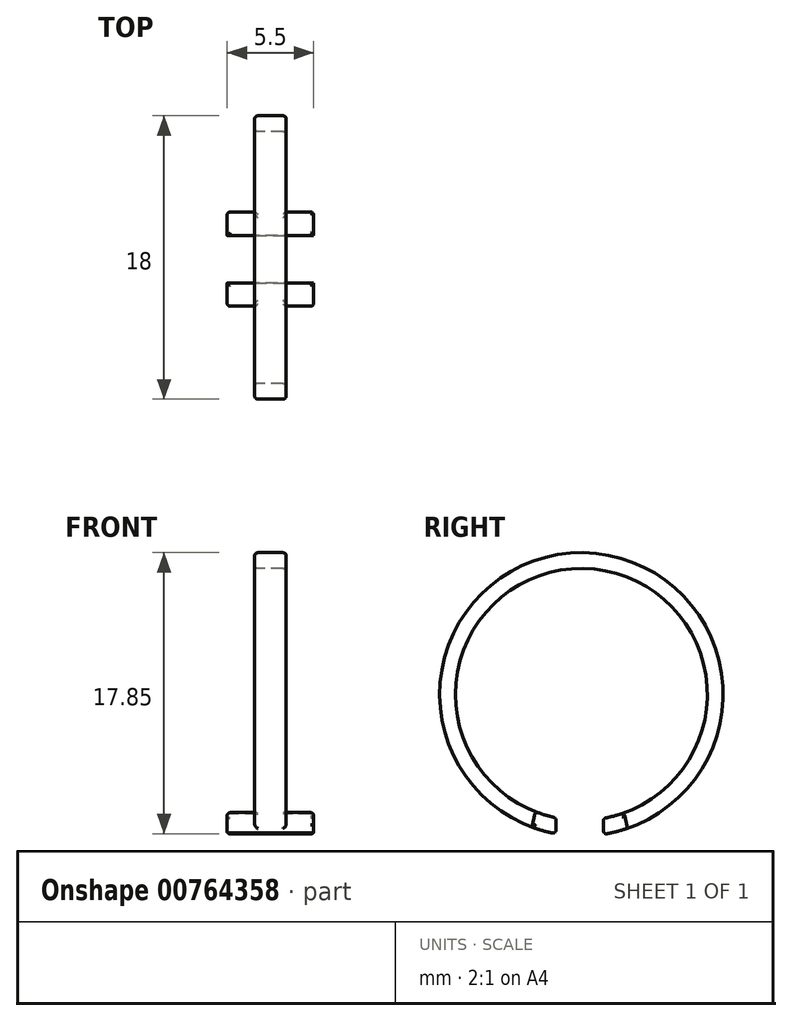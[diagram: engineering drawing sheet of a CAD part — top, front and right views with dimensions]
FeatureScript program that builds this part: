
annotation { "Feature Type Name" : "Feature", "Feature Type Description" : "" }
export const myFeature = defineFeature(function(context is Context, id is Id, definition is map)
    precondition{}
    {
        {
            var Q0;
            Q0=qCreatedBy(makeId("Right.planeOp"),FACE);
            var sketch = newSketch(context, id + "F0", { "sketchPlane" : qUnion([Q0])});
            skCircle(sketch, "E0", {"center": v(0, 0) * mm, "radius": 9 * mm});
            skSolve(sketch);
        }
        {
            var Q0;
            Q0=makeQuery(id+"F0.imprint","IMPRINT",FACE,{"disambiguationData":[TD([[makeQuery(id+"F0.imprint","IMPRINT",EDGE,{"derivedFrom":sQuery(id+"F0.wireOp",EDGE,"E0")}),1.0]])]});
            extrude(context, id + "F1", {"entities" : qUnion([Q0]), "endBound" : BoundingType.SYMMETRIC, "depth" : 2 * mm, "offsetDistance" : 25 * mm});
        }
        {
            var Q0;
            Q0=makeQuery(id+"F1.opExtrude","CAP_FACE",FACE,{"disambiguationData":[OSD([sQuery(id+"F0.wireOp",EDGE,"E0")])],"isStart":false});
            var Q1;
            Q1=makeQuery(id+"F1.opExtrude","CAP_FACE",FACE,{"disambiguationData":[OSD([sQuery(id+"F0.wireOp",EDGE,"E0")])],"isStart":true});
            shell(context, id + "F2", {"entities" : qUnion([Q0, Q1]), "thickness" : 1 * mm});
        }
        {
            var Q0;
            Q0=qCreatedBy(makeId("Right.planeOp"),FACE);
            var sketch = newSketch(context, id + "F3", { "sketchPlane" : qUnion([Q0])});
            skLineSegment(sketch, "E1", {"start": v(0, 0) * mm, "end": v(1.4, 0) * mm});
            skLineSegment(sketch, "E2", {"start": v(1.4, 0) * mm, "end": v(1.4, -10.2) * mm});
            skLineSegment(sketch, "E3", {"start": v(1.4, -10.2) * mm, "end": v(-1.6, -10.2) * mm});
            skLineSegment(sketch, "E4", {"start": v(-1.6, -10.2) * mm, "end": v(-1.6, 0) * mm});
            skLineSegment(sketch, "E5", {"start": v(-1.6, 0) * mm, "end": v(1.4, 0) * mm});
            skSolve(sketch);
        }
        {
            var Q0;
            Q0 = qSketchRegion(id + "F3", true);
            extrude(context, id + "F4", {"entities" : qUnion([Q0]), "operationType" : NewBodyOperationType.REMOVE, "endBound" : BoundingType.SYMMETRIC, "depth" : 25 * mm, "offsetDistance" : 25 * mm});
        }
        {
            var Q0;
            Q0=makeQuery(id+"F4.boolean.opBoolean","COPY",FACE,{"derivedFrom":makeQuery(id+"F4.opExtrude","SWEPT_FACE",FACE,{"disambiguationData":[OSD([sQuery(id+"F3.wireOp",EDGE,"E4")])]})});
            var sketch = newSketch(context, id + "F5", { "sketchPlane" : qUnion([Q0])});
            skLineSegment(sketch, "E6.left", {"start": v(-3, -8.13) * mm, "end": v(-3, -8.15) * mm});
            skLineSegment(sketch, "E7.bottom", {"start": v(-2.79, 8.27) * mm, "end": v(-2.76, 8.27) * mm});
            skLineSegment(sketch, "E7.top", {"start": v(-2.79, 7.32) * mm, "end": v(-2.76, 7.32) * mm});
            skLineSegment(sketch, "E7.left", {"start": v(-2.79, 8.27) * mm, "end": v(-2.79, 7.32) * mm});
            skLineSegment(sketch, "E7.right", {"start": v(-2.76, 8.27) * mm, "end": v(-2.76, 7.32) * mm});
            skLineSegment(sketch, "E8", {"start": v(1, -7.84) * mm, "end": v(-1, -8.86) * mm, "construction": true});
            skLineSegment(sketch, "E9.bottom", {"start": v(-2.75, -7.84) * mm, "end": v(2.75, -7.84) * mm});
            skLineSegment(sketch, "E9.top", {"start": v(-2.75, -8.86) * mm, "end": v(2.75, -8.86) * mm});
            skLineSegment(sketch, "E9.left", {"start": v(-2.75, -7.84) * mm, "end": v(-2.75, -8.86) * mm});
            skLineSegment(sketch, "E9.right", {"start": v(2.75, -7.84) * mm, "end": v(2.75, -8.86) * mm});
            skPoint(sketch, "E9.middle", {"position": v(0, -8.35) * mm});
            skSolve(sketch);
        }
        {
            var Q0;
            Q0=qCreatedBy(makeId("Top.planeOp"),FACE);
            var sketch = newSketch(context, id + "F6", { "sketchPlane" : qUnion([Q0])});
            skLineSegment(sketch, "E10", {"start": v(0, 0) * mm, "end": v(36.8, 0) * mm, "construction": true});
            skSolve(sketch);
        }
        {
            var Q0;
            {var subQ2=sQuery(id+"F5.wireOp",EDGE,"E9.right");Q0=makeQuery(id+"F5.imprint","IMPRINT",FACE,{"disambiguationData":[TD([[makeQuery(id+"F5.imprint","IMPRINT",EDGE,{"derivedFrom":subQ2}),-1.0]])]});}
            var Q1;
            {var subQ2=sQuery(id+"F5.wireOp",EDGE,"E9.left");Q1=makeQuery(id+"F5.imprint","IMPRINT",FACE,{"disambiguationData":[TD([[makeQuery(id+"F5.imprint","IMPRINT",EDGE,{"derivedFrom":subQ2}),1.0]])]});}
            var Q2;
            Q2=sQuery(id+"F6.wireOp",EDGE,"E10");
            revolve(context, id + "F7", {"operationType" : NewBodyOperationType.ADD, "surfaceOperationType" : NewSurfaceOperationType.NEW, "entities" : qUnion([Q0, Q1]), "axis" : qUnion([Q2]), "revolveType" : RevolveType.ONE_DIRECTION, "oppositeDirection" : true, "angle" : 10 * degree});
        }
        {
            var Q0;
            Q0=makeQuery(id+"F4.boolean.opBoolean","COPY",FACE,{"derivedFrom":makeQuery(id+"F4.opExtrude","SWEPT_FACE",FACE,{"disambiguationData":[OSD([sQuery(id+"F3.wireOp",EDGE,"E2")])]})});
            var sketch = newSketch(context, id + "F8", { "sketchPlane" : qUnion([Q0])});
            skLineSegment(sketch, "E11", {"start": v(-1, -7.88) * mm, "end": v(1, -8.9) * mm, "construction": true});
            skLineSegment(sketch, "E12.bottom", {"start": v(2.75, -8.9) * mm, "end": v(-2.75, -8.9) * mm});
            skLineSegment(sketch, "E12.top", {"start": v(2.75, -7.88) * mm, "end": v(-2.75, -7.88) * mm});
            skLineSegment(sketch, "E12.left", {"start": v(2.75, -8.9) * mm, "end": v(2.75, -7.88) * mm});
            skLineSegment(sketch, "E12.right", {"start": v(-2.75, -8.9) * mm, "end": v(-2.75, -7.88) * mm});
            skPoint(sketch, "E12.middle", {"position": v(0, -8.38) * mm});
            skSolve(sketch);
        }
        {
            var Q0;
            {var subQ2=sQuery(id+"F8.wireOp",EDGE,"E12.left");Q0=makeQuery(id+"F8.imprint","IMPRINT",FACE,{"disambiguationData":[TD([[makeQuery(id+"F8.imprint","IMPRINT",EDGE,{"derivedFrom":subQ2}),1.0]])]});}
            var Q1;
            {var subQ2=sQuery(id+"F8.wireOp",EDGE,"E12.right");Q1=makeQuery(id+"F8.imprint","IMPRINT",FACE,{"disambiguationData":[TD([[makeQuery(id+"F8.imprint","IMPRINT",EDGE,{"derivedFrom":subQ2}),-1.0]])]});}
            var Q2;
            Q2=sQuery(id+"F6.wireOp",EDGE,"E10");
            revolve(context, id + "F9", {"operationType" : NewBodyOperationType.ADD, "surfaceOperationType" : NewSurfaceOperationType.NEW, "entities" : qUnion([Q0, Q1]), "axis" : qUnion([Q2]), "revolveType" : RevolveType.ONE_DIRECTION, "angle" : 10 * degree});
        }
        {
            var Q0;
            {var subQ0=sQuery(id+"F0.wireOp",EDGE,"E0");Q0=makeQuery(id+"F2.opShell","OFFSET_EDGE",EDGE,{"disambiguationData":[OSD([subQ0]),TDD([makeQuery(id+"F1.opExtrude","CAP_EDGE",EDGE,{"disambiguationData":[OSD([subQ0])],"isStart":false})])]});}
            var Q1;
            Q1=makeQuery(id+"F9.opRevolve","SWEPT_EDGE",EDGE,{"disambiguationData":[OSD([sQuery(id+"F8.wireOp",EDGE,"E12.bottom"),sQuery(id+"F8.wireOp",EDGE,"E12.right")])]});
            var Q2;
            Q2=makeQuery(id+"F9.opRevolve","SWEPT_EDGE",EDGE,{"disambiguationData":[OSD([sQuery(id+"F8.wireOp",EDGE,"E12.top"),sQuery(id+"F8.wireOp",EDGE,"E12.left")])]});
            var Q3;
            Q3=makeQuery(id+"F7.opRevolve","SWEPT_EDGE",EDGE,{"disambiguationData":[OSD([sQuery(id+"F5.wireOp",EDGE,"E9.top"),sQuery(id+"F5.wireOp",EDGE,"E9.left")])]});
            var Q4;
            Q4=makeQuery(id+"F9.opRevolve","SWEPT_EDGE",EDGE,{"disambiguationData":[OSD([sQuery(id+"F8.wireOp",EDGE,"E12.bottom"),sQuery(id+"F8.wireOp",EDGE,"E12.left")])]});
            var Q5;
            {var subQ0=sQuery(id+"F5.wireOp",EDGE,"E9.bottom");var subQ1=makeQuery(id+"F4.opExtrude","SWEPT_FACE",FACE,{"disambiguationData":[OSD([sQuery(id+"F3.wireOp",EDGE,"E4")])]});var subQ2=sQuery(id+"F0.wireOp",EDGE,"E0");Q5=makeQuery(id+"F7.boolean.opBoolean","MERGE",EDGE,{"derivedFrom":[makeQuery(id+"F4.boolean.opBoolean","INTERSECT",EDGE,{"derivedFrom":[makeQuery(id+"F2.opShell","OFFSET_FACE",FACE,{"disambiguationData":[OSD([subQ2])]}),subQ1]}),makeQuery(id+"F7.opRevolve","CAP_EDGE",EDGE,{"disambiguationData":[OSD([subQ0]),TDD([makeQuery(id+"F5.imprint","IMPRINT",EDGE,{"disambiguationData":[TD([[makeQuery(id+"F5.imprint","INTERSECT",VERTEX,{"derivedFrom":[makeQuery(id+"F4.boolean.opBoolean","INTERSECT",EDGE,{"derivedFrom":[makeQuery(id+"F1.opExtrude","CAP_FACE",FACE,{"disambiguationData":[OSD([subQ2])],"isStart":false}),subQ1]}),subQ0]}),1.0],[makeQuery(id+"F5.imprint","INTERSECT",VERTEX,{"derivedFrom":[subQ0,sQuery(id+"F5.wireOp",EDGE,"E9.left")]}),-1.0]])],"derivedFrom":subQ0})]),OD(0.0)],"isStart":false}),makeQuery(id+"F7.opRevolve","CAP_EDGE",EDGE,{"disambiguationData":[OSD([subQ0]),TDD([makeQuery(id+"F5.imprint","IMPRINT",EDGE,{"disambiguationData":[TD([[makeQuery(id+"F5.imprint","INTERSECT",VERTEX,{"derivedFrom":[makeQuery(id+"F4.boolean.opBoolean","INTERSECT",EDGE,{"derivedFrom":[makeQuery(id+"F1.opExtrude","CAP_FACE",FACE,{"disambiguationData":[OSD([subQ2])],"isStart":true}),subQ1]}),subQ0]}),-1.0],[makeQuery(id+"F5.imprint","INTERSECT",VERTEX,{"derivedFrom":[subQ0,sQuery(id+"F5.wireOp",EDGE,"E9.right")]}),1.0]])],"derivedFrom":subQ0})]),OD(0.0)],"isStart":false})]});}
            var Q6;
            Q6=makeQuery(id+"F7.opRevolve","SWEPT_EDGE",EDGE,{"disambiguationData":[OSD([sQuery(id+"F5.wireOp",EDGE,"E9.top"),sQuery(id+"F5.wireOp",EDGE,"E9.right")])]});
            var Q7;
            {var subQ0=sQuery(id+"F5.wireOp",EDGE,"E9.top");var subQ1=makeQuery(id+"F4.opExtrude","SWEPT_FACE",FACE,{"disambiguationData":[OSD([sQuery(id+"F3.wireOp",EDGE,"E4")])]});var subQ2=sQuery(id+"F0.wireOp",EDGE,"E0");Q7=makeQuery(id+"F7.boolean.opBoolean","MERGE",EDGE,{"derivedFrom":[makeQuery(id+"F4.boolean.opBoolean","INTERSECT",EDGE,{"derivedFrom":[makeQuery(id+"F1.opExtrude","SWEPT_FACE",FACE,{"disambiguationData":[OSD([subQ2])]}),subQ1]}),makeQuery(id+"F7.opRevolve","CAP_EDGE",EDGE,{"disambiguationData":[OSD([subQ0]),TDD([makeQuery(id+"F5.imprint","IMPRINT",EDGE,{"disambiguationData":[TD([[makeQuery(id+"F5.imprint","INTERSECT",VERTEX,{"derivedFrom":[makeQuery(id+"F4.boolean.opBoolean","INTERSECT",EDGE,{"derivedFrom":[makeQuery(id+"F1.opExtrude","CAP_FACE",FACE,{"disambiguationData":[OSD([subQ2])],"isStart":false}),subQ1]}),subQ0]}),1.0],[makeQuery(id+"F5.imprint","INTERSECT",VERTEX,{"derivedFrom":[subQ0,sQuery(id+"F5.wireOp",EDGE,"E9.left")]}),-1.0]])],"derivedFrom":subQ0})]),OD(0.0)],"isStart":false}),makeQuery(id+"F7.opRevolve","CAP_EDGE",EDGE,{"disambiguationData":[OSD([subQ0]),TDD([makeQuery(id+"F5.imprint","IMPRINT",EDGE,{"disambiguationData":[TD([[makeQuery(id+"F5.imprint","INTERSECT",VERTEX,{"derivedFrom":[makeQuery(id+"F4.boolean.opBoolean","INTERSECT",EDGE,{"derivedFrom":[makeQuery(id+"F1.opExtrude","CAP_FACE",FACE,{"disambiguationData":[OSD([subQ2])],"isStart":true}),subQ1]}),subQ0]}),-1.0],[makeQuery(id+"F5.imprint","INTERSECT",VERTEX,{"derivedFrom":[subQ0,sQuery(id+"F5.wireOp",EDGE,"E9.right")]}),1.0]])],"derivedFrom":subQ0})]),OD(0.0)],"isStart":false})]});}
            var Q8;
            Q8=makeQuery(id+"F7.opRevolve","SWEPT_EDGE",EDGE,{"disambiguationData":[OSD([sQuery(id+"F5.wireOp",EDGE,"E9.bottom"),sQuery(id+"F5.wireOp",EDGE,"E9.left")])]});
            var Q9;
            Q9=makeQuery(id+"F7.opRevolve","CAP_EDGE",EDGE,{"disambiguationData":[OSD([sQuery(id+"F5.wireOp",EDGE,"E9.left")]),OD(0.0)],"isStart":false});
            var Q10;
            {var subQ0=sQuery(id+"F0.wireOp",EDGE,"E0");Q10=makeQuery(id+"F2.opShell","OFFSET_EDGE",EDGE,{"disambiguationData":[OSD([subQ0]),TDD([makeQuery(id+"F1.opExtrude","CAP_EDGE",EDGE,{"disambiguationData":[OSD([subQ0])],"isStart":true})])]});}
            var Q11;
            Q11=makeQuery(id+"F1.opExtrude","CAP_EDGE",EDGE,{"disambiguationData":[OSD([sQuery(id+"F0.wireOp",EDGE,"E0")])],"isStart":false});
            var Q12;
            Q12=makeQuery(id+"F1.opExtrude","CAP_EDGE",EDGE,{"disambiguationData":[OSD([sQuery(id+"F0.wireOp",EDGE,"E0")])],"isStart":true});
            var Q13;
            {var subQ0=sQuery(id+"F8.wireOp",EDGE,"E12.bottom");var subQ1=makeQuery(id+"F4.opExtrude","SWEPT_FACE",FACE,{"disambiguationData":[OSD([sQuery(id+"F3.wireOp",EDGE,"E2")])]});var subQ2=sQuery(id+"F0.wireOp",EDGE,"E0");Q13=makeQuery(id+"F9.boolean.opBoolean","MERGE",EDGE,{"derivedFrom":[makeQuery(id+"F4.boolean.opBoolean","INTERSECT",EDGE,{"derivedFrom":[makeQuery(id+"F1.opExtrude","SWEPT_FACE",FACE,{"disambiguationData":[OSD([subQ2])]}),subQ1]}),makeQuery(id+"F9.opRevolve","CAP_EDGE",EDGE,{"disambiguationData":[OSD([subQ0]),TDD([makeQuery(id+"F8.imprint","IMPRINT",EDGE,{"disambiguationData":[TD([[makeQuery(id+"F8.imprint","INTERSECT",VERTEX,{"derivedFrom":[subQ0,sQuery(id+"F8.wireOp",EDGE,"E12.left")]}),-1.0]])],"derivedFrom":subQ0})]),OD(0.0)],"isStart":false}),makeQuery(id+"F9.opRevolve","CAP_EDGE",EDGE,{"disambiguationData":[OSD([subQ0]),TDD([makeQuery(id+"F8.imprint","IMPRINT",EDGE,{"disambiguationData":[TD([[makeQuery(id+"F8.imprint","INTERSECT",VERTEX,{"derivedFrom":[subQ0,sQuery(id+"F8.wireOp",EDGE,"E12.right")]}),1.0]])],"derivedFrom":subQ0})]),OD(0.0)],"isStart":false})]});}
            var Q14;
            {var subQ0=sQuery(id+"F5.wireOp",EDGE,"E9.bottom");Q14=makeQuery(id+"F7.opRevolve","CAP_EDGE",EDGE,{"disambiguationData":[OSD([subQ0]),TDD([makeQuery(id+"F5.imprint","IMPRINT",EDGE,{"disambiguationData":[TD([[makeQuery(id+"F5.imprint","INTERSECT",VERTEX,{"derivedFrom":[makeQuery(id+"F4.boolean.opBoolean","INTERSECT",EDGE,{"derivedFrom":[makeQuery(id+"F1.opExtrude","CAP_FACE",FACE,{"disambiguationData":[OSD([sQuery(id+"F0.wireOp",EDGE,"E0")])],"isStart":true}),makeQuery(id+"F4.opExtrude","SWEPT_FACE",FACE,{"disambiguationData":[OSD([sQuery(id+"F3.wireOp",EDGE,"E4")])]})]}),subQ0]}),-1.0],[makeQuery(id+"F5.imprint","INTERSECT",VERTEX,{"derivedFrom":[subQ0,sQuery(id+"F5.wireOp",EDGE,"E9.right")]}),1.0]])],"derivedFrom":subQ0})]),OD(1.0)],"isStart":false});}
            var Q15;
            {var subQ0=sQuery(id+"F8.wireOp",EDGE,"E12.top");Q15=makeQuery(id+"F9.opRevolve","CAP_EDGE",EDGE,{"disambiguationData":[OSD([subQ0]),TDD([makeQuery(id+"F8.imprint","IMPRINT",EDGE,{"disambiguationData":[TD([[makeQuery(id+"F8.imprint","INTERSECT",VERTEX,{"derivedFrom":[subQ0,sQuery(id+"F8.wireOp",EDGE,"E12.left")]}),-1.0]])],"derivedFrom":subQ0})]),OD(1.0)],"isStart":false});}
            var Q16;
            Q16=makeQuery(id+"F9.opRevolve","SWEPT_EDGE",EDGE,{"disambiguationData":[OSD([sQuery(id+"F8.wireOp",EDGE,"E12.top"),sQuery(id+"F8.wireOp",EDGE,"E12.right")])]});
            var Q17;
            {var subQ0=sQuery(id+"F5.wireOp",EDGE,"E9.top");Q17=makeQuery(id+"F7.opRevolve","CAP_EDGE",EDGE,{"disambiguationData":[OSD([subQ0]),TDD([makeQuery(id+"F5.imprint","IMPRINT",EDGE,{"disambiguationData":[TD([[makeQuery(id+"F5.imprint","INTERSECT",VERTEX,{"derivedFrom":[makeQuery(id+"F4.boolean.opBoolean","INTERSECT",EDGE,{"derivedFrom":[makeQuery(id+"F1.opExtrude","CAP_FACE",FACE,{"disambiguationData":[OSD([sQuery(id+"F0.wireOp",EDGE,"E0")])],"isStart":false}),makeQuery(id+"F4.opExtrude","SWEPT_FACE",FACE,{"disambiguationData":[OSD([sQuery(id+"F3.wireOp",EDGE,"E4")])]})]}),subQ0]}),1.0],[makeQuery(id+"F5.imprint","INTERSECT",VERTEX,{"derivedFrom":[subQ0,sQuery(id+"F5.wireOp",EDGE,"E9.left")]}),-1.0]])],"derivedFrom":subQ0})]),OD(1.0)],"isStart":false});}
            var Q18;
            {var subQ0=sQuery(id+"F8.wireOp",EDGE,"E12.top");Q18=makeQuery(id+"F9.opRevolve","CAP_EDGE",EDGE,{"disambiguationData":[OSD([subQ0]),TDD([makeQuery(id+"F8.imprint","IMPRINT",EDGE,{"disambiguationData":[TD([[makeQuery(id+"F8.imprint","INTERSECT",VERTEX,{"derivedFrom":[subQ0,sQuery(id+"F8.wireOp",EDGE,"E12.right")]}),1.0]])],"derivedFrom":subQ0})]),OD(1.0)],"isStart":false});}
            var Q19;
            Q19=makeQuery(id+"F7.opRevolve","CAP_EDGE",EDGE,{"disambiguationData":[OSD([sQuery(id+"F5.wireOp",EDGE,"E9.right")]),OD(0.0)],"isStart":false});
            var Q20;
            Q20=makeQuery(id+"F9.opRevolve","CAP_EDGE",EDGE,{"disambiguationData":[OSD([sQuery(id+"F8.wireOp",EDGE,"E12.right")]),OD(0.0)],"isStart":false});
            var Q21;
            Q21=makeQuery(id+"F7.opRevolve","SWEPT_EDGE",EDGE,{"disambiguationData":[OSD([sQuery(id+"F5.wireOp",EDGE,"E9.bottom"),sQuery(id+"F5.wireOp",EDGE,"E9.right")])]});
            var Q22;
            {var subQ0=sQuery(id+"F5.wireOp",EDGE,"E9.top");Q22=makeQuery(id+"F7.opRevolve","CAP_EDGE",EDGE,{"disambiguationData":[OSD([subQ0]),TDD([makeQuery(id+"F5.imprint","IMPRINT",EDGE,{"disambiguationData":[TD([[makeQuery(id+"F5.imprint","INTERSECT",VERTEX,{"derivedFrom":[makeQuery(id+"F4.boolean.opBoolean","INTERSECT",EDGE,{"derivedFrom":[makeQuery(id+"F1.opExtrude","CAP_FACE",FACE,{"disambiguationData":[OSD([sQuery(id+"F0.wireOp",EDGE,"E0")])],"isStart":true}),makeQuery(id+"F4.opExtrude","SWEPT_FACE",FACE,{"disambiguationData":[OSD([sQuery(id+"F3.wireOp",EDGE,"E4")])]})]}),subQ0]}),-1.0],[makeQuery(id+"F5.imprint","INTERSECT",VERTEX,{"derivedFrom":[subQ0,sQuery(id+"F5.wireOp",EDGE,"E9.right")]}),1.0]])],"derivedFrom":subQ0})]),OD(1.0)],"isStart":false});}
            var Q23;
            {var subQ0=sQuery(id+"F5.wireOp",EDGE,"E9.bottom");Q23=makeQuery(id+"F7.opRevolve","CAP_EDGE",EDGE,{"disambiguationData":[OSD([subQ0]),TDD([makeQuery(id+"F5.imprint","IMPRINT",EDGE,{"disambiguationData":[TD([[makeQuery(id+"F5.imprint","INTERSECT",VERTEX,{"derivedFrom":[makeQuery(id+"F4.boolean.opBoolean","INTERSECT",EDGE,{"derivedFrom":[makeQuery(id+"F1.opExtrude","CAP_FACE",FACE,{"disambiguationData":[OSD([sQuery(id+"F0.wireOp",EDGE,"E0")])],"isStart":false}),makeQuery(id+"F4.opExtrude","SWEPT_FACE",FACE,{"disambiguationData":[OSD([sQuery(id+"F3.wireOp",EDGE,"E4")])]})]}),subQ0]}),1.0],[makeQuery(id+"F5.imprint","INTERSECT",VERTEX,{"derivedFrom":[subQ0,sQuery(id+"F5.wireOp",EDGE,"E9.left")]}),-1.0]])],"derivedFrom":subQ0})]),OD(1.0)],"isStart":false});}
            var Q24;
            {var subQ0=sQuery(id+"F8.wireOp",EDGE,"E12.top");var subQ1=makeQuery(id+"F4.opExtrude","SWEPT_FACE",FACE,{"disambiguationData":[OSD([sQuery(id+"F3.wireOp",EDGE,"E2")])]});var subQ2=sQuery(id+"F0.wireOp",EDGE,"E0");Q24=makeQuery(id+"F9.boolean.opBoolean","MERGE",EDGE,{"derivedFrom":[makeQuery(id+"F4.boolean.opBoolean","INTERSECT",EDGE,{"derivedFrom":[makeQuery(id+"F2.opShell","OFFSET_FACE",FACE,{"disambiguationData":[OSD([subQ2])]}),subQ1]}),makeQuery(id+"F9.opRevolve","CAP_EDGE",EDGE,{"disambiguationData":[OSD([subQ0]),TDD([makeQuery(id+"F8.imprint","IMPRINT",EDGE,{"disambiguationData":[TD([[makeQuery(id+"F8.imprint","INTERSECT",VERTEX,{"derivedFrom":[subQ0,sQuery(id+"F8.wireOp",EDGE,"E12.left")]}),-1.0]])],"derivedFrom":subQ0})]),OD(0.0)],"isStart":false}),makeQuery(id+"F9.opRevolve","CAP_EDGE",EDGE,{"disambiguationData":[OSD([subQ0]),TDD([makeQuery(id+"F8.imprint","IMPRINT",EDGE,{"disambiguationData":[TD([[makeQuery(id+"F8.imprint","INTERSECT",VERTEX,{"derivedFrom":[subQ0,sQuery(id+"F8.wireOp",EDGE,"E12.right")]}),1.0]])],"derivedFrom":subQ0})]),OD(0.0)],"isStart":false})]});}
            var Q25;
            {var subQ0=sQuery(id+"F8.wireOp",EDGE,"E12.bottom");Q25=makeQuery(id+"F9.opRevolve","CAP_EDGE",EDGE,{"disambiguationData":[OSD([subQ0]),TDD([makeQuery(id+"F8.imprint","IMPRINT",EDGE,{"disambiguationData":[TD([[makeQuery(id+"F8.imprint","INTERSECT",VERTEX,{"derivedFrom":[subQ0,sQuery(id+"F8.wireOp",EDGE,"E12.right")]}),1.0]])],"derivedFrom":subQ0})]),OD(1.0)],"isStart":false});}
            var Q26;
            Q26=makeQuery(id+"F9.opRevolve","CAP_EDGE",EDGE,{"disambiguationData":[OSD([sQuery(id+"F8.wireOp",EDGE,"E12.left")]),OD(0.0)],"isStart":false});
            var Q27;
            Q27=makeQuery(id+"F9.opRevolve","CAP_EDGE",EDGE,{"disambiguationData":[OSD([sQuery(id+"F8.wireOp",EDGE,"E12.left")]),OD(1.0)],"isStart":false});
            var Q28;
            {var subQ0=sQuery(id+"F3.wireOp",EDGE,"E2");var subQ1=sQuery(id+"F0.wireOp",EDGE,"E0");Q28=makeQuery(id+"F9.opRevolve","CAP_EDGE",EDGE,{"disambiguationData":[OSD([subQ1,subQ0]),TDD([makeQuery(id+"F8.imprint","IMPRINT",EDGE,{"derivedFrom":makeQuery(id+"F4.boolean.opBoolean","INTERSECT",EDGE,{"derivedFrom":[makeQuery(id+"F1.opExtrude","CAP_FACE",FACE,{"disambiguationData":[OSD([subQ1])],"isStart":false}),makeQuery(id+"F4.opExtrude","SWEPT_FACE",FACE,{"disambiguationData":[OSD([subQ0])]})]})})]),OD(1.0)],"isStart":false});}
            var Q29;
            {var subQ0=sQuery(id+"F8.wireOp",EDGE,"E12.bottom");Q29=makeQuery(id+"F9.opRevolve","CAP_EDGE",EDGE,{"disambiguationData":[OSD([subQ0]),TDD([makeQuery(id+"F8.imprint","IMPRINT",EDGE,{"disambiguationData":[TD([[makeQuery(id+"F8.imprint","INTERSECT",VERTEX,{"derivedFrom":[subQ0,sQuery(id+"F8.wireOp",EDGE,"E12.left")]}),-1.0]])],"derivedFrom":subQ0})]),OD(1.0)],"isStart":false});}
            var Q30;
            {var subQ0=sQuery(id+"F3.wireOp",EDGE,"E4");var subQ1=sQuery(id+"F0.wireOp",EDGE,"E0");Q30=makeQuery(id+"F7.opRevolve","CAP_EDGE",EDGE,{"disambiguationData":[OSD([subQ1,subQ0]),TDD([makeQuery(id+"F5.imprint","IMPRINT",EDGE,{"derivedFrom":makeQuery(id+"F4.boolean.opBoolean","INTERSECT",EDGE,{"derivedFrom":[makeQuery(id+"F1.opExtrude","CAP_FACE",FACE,{"disambiguationData":[OSD([subQ1])],"isStart":true}),makeQuery(id+"F4.opExtrude","SWEPT_FACE",FACE,{"disambiguationData":[OSD([subQ0])]})]})})]),OD(1.0)],"isStart":false});}
            var Q31;
            Q31=makeQuery(id+"F7.opRevolve","CAP_EDGE",EDGE,{"disambiguationData":[OSD([sQuery(id+"F5.wireOp",EDGE,"E9.left")]),OD(1.0)],"isStart":false});
            var Q32;
            Q32=makeQuery(id+"F9.opRevolve","CAP_EDGE",EDGE,{"disambiguationData":[OSD([sQuery(id+"F8.wireOp",EDGE,"E12.right")]),OD(1.0)],"isStart":false});
            var Q33;
            {var subQ0=sQuery(id+"F3.wireOp",EDGE,"E4");var subQ1=sQuery(id+"F0.wireOp",EDGE,"E0");Q33=makeQuery(id+"F7.opRevolve","CAP_EDGE",EDGE,{"disambiguationData":[OSD([subQ1,subQ0]),TDD([makeQuery(id+"F5.imprint","IMPRINT",EDGE,{"derivedFrom":makeQuery(id+"F4.boolean.opBoolean","INTERSECT",EDGE,{"derivedFrom":[makeQuery(id+"F1.opExtrude","CAP_FACE",FACE,{"disambiguationData":[OSD([subQ1])],"isStart":false}),makeQuery(id+"F4.opExtrude","SWEPT_FACE",FACE,{"disambiguationData":[OSD([subQ0])]})]})})]),OD(1.0)],"isStart":false});}
            var Q34;
            Q34=makeQuery(id+"F7.opRevolve","CAP_EDGE",EDGE,{"disambiguationData":[OSD([sQuery(id+"F5.wireOp",EDGE,"E9.right")]),OD(1.0)],"isStart":false});
            var Q35;
            {var subQ0=sQuery(id+"F3.wireOp",EDGE,"E2");var subQ1=sQuery(id+"F0.wireOp",EDGE,"E0");Q35=makeQuery(id+"F9.opRevolve","CAP_EDGE",EDGE,{"disambiguationData":[OSD([subQ1,subQ0]),TDD([makeQuery(id+"F8.imprint","IMPRINT",EDGE,{"derivedFrom":makeQuery(id+"F4.boolean.opBoolean","INTERSECT",EDGE,{"derivedFrom":[makeQuery(id+"F1.opExtrude","CAP_FACE",FACE,{"disambiguationData":[OSD([subQ1])],"isStart":true}),makeQuery(id+"F4.opExtrude","SWEPT_FACE",FACE,{"disambiguationData":[OSD([subQ0])]})]})})]),OD(1.0)],"isStart":false});}
            fillet(context, id + "F10", {"entities" : qUnion([Q0, Q1, Q2, Q3, Q4, Q5, Q6, Q7, Q8, Q9, Q10, Q11, Q12, Q13, Q14, Q15, Q16, Q17, Q18, Q19, Q20, Q21, Q22, Q23, Q24, Q25, Q26, Q27, Q28, Q29, Q30, Q31, Q32, Q33, Q34, Q35]), "radius" : .2 * mm, "tangentPropagation" : true, "allowEdgeOverflow" : false});
        }
    });
